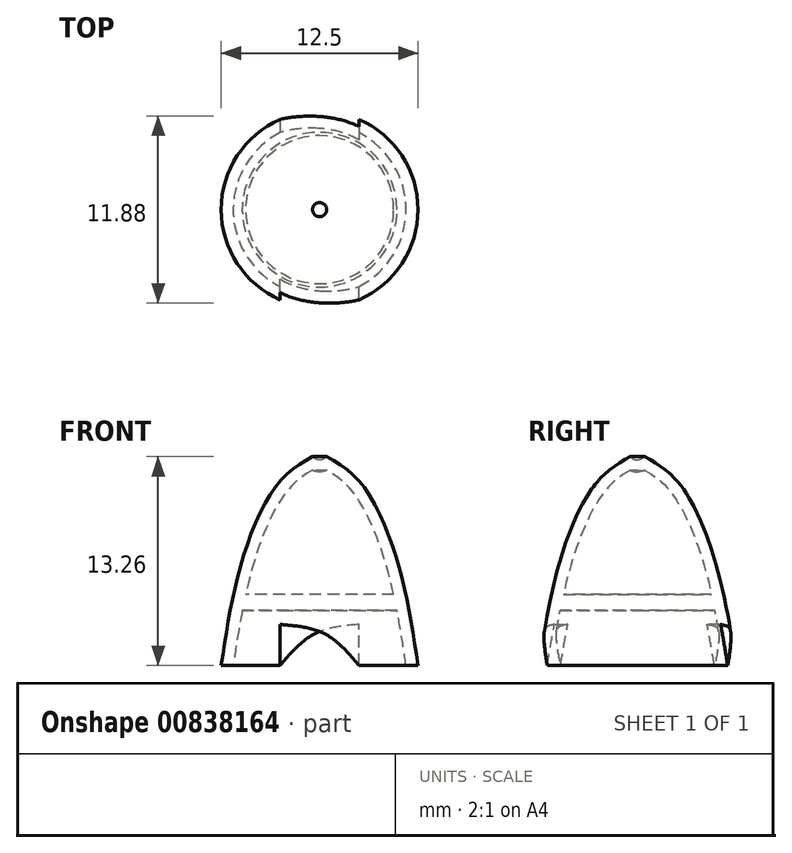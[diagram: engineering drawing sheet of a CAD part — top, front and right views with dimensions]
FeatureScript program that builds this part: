
annotation { "Feature Type Name" : "Feature", "Feature Type Description" : "" }
export const myFeature = defineFeature(function(context is Context, id is Id, definition is map)
    precondition{}
    {
        {
            var Q0;
            Q0=qCreatedBy(makeId("Front.planeOp"),FACE);
            var sketch = newSketch(context, id + "F0", { "sketchPlane" : qUnion([Q0])});
            skLineSegment(sketch, "E0", {"start": v(-43.41, 9) * mm, "end": v(47.35, 9) * mm, "construction": true});
            skLineSegment(sketch, "E1", {"start": v(-24.44, 13.5) * mm, "end": v(23.13, 13.5) * mm, "construction": true});
            skLineSegment(sketch, "E2", {"start": v(-44.29, 4.5) * mm, "end": v(45.3, 4.5) * mm, "construction": true});
            skPoint(sketch, "E3", {"position": v(-6.25, 0) * mm});
            skPoint(sketch, "E4", {"position": v(-4.9, 4.5) * mm});
            skPoint(sketch, "E5", {"position": v(-3.25, 9) * mm});
            skPoint(sketch, "E6", {"position": v(-1, 13.5) * mm});
            skLineSegment(sketch, "E7", {"start": v(0, 0) * mm, "end": v(-6.25, 0) * mm});
            skLineSegment(sketch, "E8", {"start": v(-2.5, 0) * mm, "end": v(-2.5, 2.6) * mm});
            skPoint(sketch, "E9", {"position": v(2.5, 0) * mm});
            skFitSpline(sketch, "E10", {"points": [v(-2.5, 2.6) * mm, v(0.33, 2) * mm, v(2.5, 0) * mm], "startDerivative": vector(6.02, -0.52) * mm, "endDerivative": vector(3.98, -4.68) * mm});
            skLineSegment(sketch, "E11", {"start": v(0, 0) * mm, "end": v(2.5, 0) * mm});
            skLineSegment(sketch, "E12", {"start": v(0, 13.04) * mm, "end": v(0, 0) * mm});
            skFitSpline(sketch, "E13.MirrorCS", {"points": [v(2.5, 2.6) * mm, v(-0.33, 2) * mm, v(-2.5, 0) * mm], "startDerivative": vector(-6.02, -0.52) * mm, "endDerivative": vector(-3.98, -4.68) * mm});
            skLineSegment(sketch, "E14.MirrorCS", {"start": v(2.5, 0) * mm, "end": v(2.5, 2.6) * mm});
            skPoint(sketch, "E15.end.orphan", {"position": v(0, 13.5) * mm});
            skFitSpline(sketch, "E16", {"points": [v(-6.25, 0) * mm, v(-5.01, 6.36) * mm, v(-2.54, 11.67) * mm, v(0, 13.5) * mm], "startDerivative": vector(2.51, 16.76) * mm, "endDerivative": vector(10.12, 5.28) * mm});
            skFitSpline(sketch, "E17", {"points": [v(0, 13.04) * mm, v(-0.25, 13.1) * mm, v(-0.45, 13.26) * mm], "startDerivative": vector(-0.51, 0.08) * mm, "endDerivative": vector(-0.38, 0.36) * mm});
            skPoint(sketch, "E18.MirrorP", {"position": v(4.9, 4.5) * mm});
            skLineSegment(sketch, "E19", {"start": v(4.9, 4.5) * mm, "end": v(0, 4.5) * mm});
            skLineSegment(sketch, "E20", {"start": v(0, 4.5) * mm, "end": v(0, 3.5) * mm});
            skLineSegment(sketch, "E21", {"start": v(0, 3.5) * mm, "end": v(5, 3.5) * mm});
            skLineSegment(sketch, "E22", {"start": v(5, 3.5) * mm, "end": v(4.9, 4.5) * mm});
            skSolve(sketch);
        }
        {
            var Q0;
            {var subQ5=sQuery(id+"F0.wireOp",EDGE,"E8");Q0=makeQuery(id+"F0.imprint","IMPRINT",FACE,{"disambiguationData":[TD([[makeQuery(id+"F0.imprint","IMPRINT",EDGE,{"derivedFrom":subQ5}),1.0]])]});}
            var Q1;
            {var subQ0=sQuery(id+"F0.wireOp",EDGE,"E8");Q1=makeQuery(id+"F0.imprint","IMPRINT",FACE,{"disambiguationData":[TD([[makeQuery(id+"F0.imprint","IMPRINT",EDGE,{"derivedFrom":subQ0}),-1.0]])]});}
            var Q2;
            {var subQ0=sQuery(id+"F0.wireOp",EDGE,"E13.MirrorCS");var subQ1=sQuery(id+"F0.wireOp",EDGE,"E7");var subQ2=makeQuery(id+"F0.imprint","INTERSECT",VERTEX,{"derivedFrom":[subQ1,sQuery(id+"F0.wireOp",EDGE,"E8"),subQ0]});Q2=makeQuery(id+"F0.imprint","IMPRINT",FACE,{"disambiguationData":[TD([[makeQuery(id+"F0.imprint","IMPRINT",EDGE,{"disambiguationData":[TD([[subQ2,1.0]])],"derivedFrom":subQ1}),-1.0]])]});}
            var Q3;
            Q3=sQuery(id+"F0.wireOp",EDGE,"E12");
            revolve(context, id + "F1", {"surfaceOperationType" : NewSurfaceOperationType.NEW, "entities" : qUnion([Q0, Q1, Q2]), "axis" : qUnion([Q3]), "revolveType" : RevolveType.FULL});
        }
        {
            var Q0;
            Q0=makeQuery(id+"F1.opRevolve","SWEPT_FACE",FACE,{"disambiguationData":[OSD([sQuery(id+"F0.wireOp",EDGE,"E7")])]});
            shell(context, id + "F2", {"entities" : qUnion([Q0]), "thickness" : 0.75 * mm});
        }
        {
            var Q0;
            {var subQ0=sQuery(id+"F0.wireOp",EDGE,"E8");Q0=makeQuery(id+"F0.imprint","IMPRINT",FACE,{"disambiguationData":[TD([[makeQuery(id+"F0.imprint","IMPRINT",EDGE,{"derivedFrom":subQ0}),-1.0]])]});}
            var Q1;
            {var subQ0=sQuery(id+"F0.wireOp",EDGE,"E13.MirrorCS");var subQ1=sQuery(id+"F0.wireOp",EDGE,"E7");var subQ2=makeQuery(id+"F0.imprint","INTERSECT",VERTEX,{"derivedFrom":[subQ1,sQuery(id+"F0.wireOp",EDGE,"E8"),subQ0]});Q1=makeQuery(id+"F0.imprint","IMPRINT",FACE,{"disambiguationData":[TD([[makeQuery(id+"F0.imprint","IMPRINT",EDGE,{"disambiguationData":[TD([[subQ2,1.0]])],"derivedFrom":subQ1}),-1.0]])]});}
            var Q2;
            {var subQ0=sQuery(id+"F0.wireOp",EDGE,"E11");Q2=makeQuery(id+"F0.imprint","IMPRINT",FACE,{"disambiguationData":[TD([[makeQuery(id+"F0.imprint","IMPRINT",EDGE,{"derivedFrom":subQ0}),1.0]])]});}
            extrude(context, id + "F3", {"entities" : qUnion([Q0, Q1, Q2]), "operationType" : NewBodyOperationType.REMOVE, "depth" : 25 * mm, "offsetDistance" : 25 * mm});
        }
        {
            var Q0;
            {var subQ0=sQuery(id+"F0.wireOp",EDGE,"E14.MirrorCS");Q0=makeQuery(id+"F0.imprint","IMPRINT",FACE,{"disambiguationData":[TD([[makeQuery(id+"F0.imprint","IMPRINT",EDGE,{"derivedFrom":subQ0}),1.0]])]});}
            var Q1;
            {var subQ0=sQuery(id+"F0.wireOp",EDGE,"E11");Q1=makeQuery(id+"F0.imprint","IMPRINT",FACE,{"disambiguationData":[TD([[makeQuery(id+"F0.imprint","IMPRINT",EDGE,{"derivedFrom":subQ0}),1.0]])]});}
            var Q2;
            {var subQ0=sQuery(id+"F0.wireOp",EDGE,"E13.MirrorCS");var subQ1=sQuery(id+"F0.wireOp",EDGE,"E7");var subQ2=makeQuery(id+"F0.imprint","INTERSECT",VERTEX,{"derivedFrom":[subQ1,sQuery(id+"F0.wireOp",EDGE,"E8"),subQ0]});Q2=makeQuery(id+"F0.imprint","IMPRINT",FACE,{"disambiguationData":[TD([[makeQuery(id+"F0.imprint","IMPRINT",EDGE,{"disambiguationData":[TD([[subQ2,1.0]])],"derivedFrom":subQ1}),-1.0]])]});}
            extrude(context, id + "F4", {"entities" : qUnion([Q0, Q1, Q2]), "operationType" : NewBodyOperationType.REMOVE, "oppositeDirection" : true, "depth" : 25 * mm, "offsetDistance" : 25 * mm});
        }
        {
            var Q0;
            {var subQ2=sQuery(id+"F0.wireOp",EDGE,"E19");Q0=makeQuery(id+"F0.imprint","IMPRINT",FACE,{"disambiguationData":[TD([[makeQuery(id+"F0.imprint","IMPRINT",EDGE,{"derivedFrom":subQ2}),1.0]])]});}
            var Q1;
            Q1=sQuery(id+"F0.wireOp",EDGE,"E12");
            revolve(context, id + "F5", {"operationType" : NewBodyOperationType.ADD, "surfaceOperationType" : NewSurfaceOperationType.NEW, "entities" : qUnion([Q0]), "axis" : qUnion([Q1]), "revolveType" : RevolveType.FULL});
        }
    });
